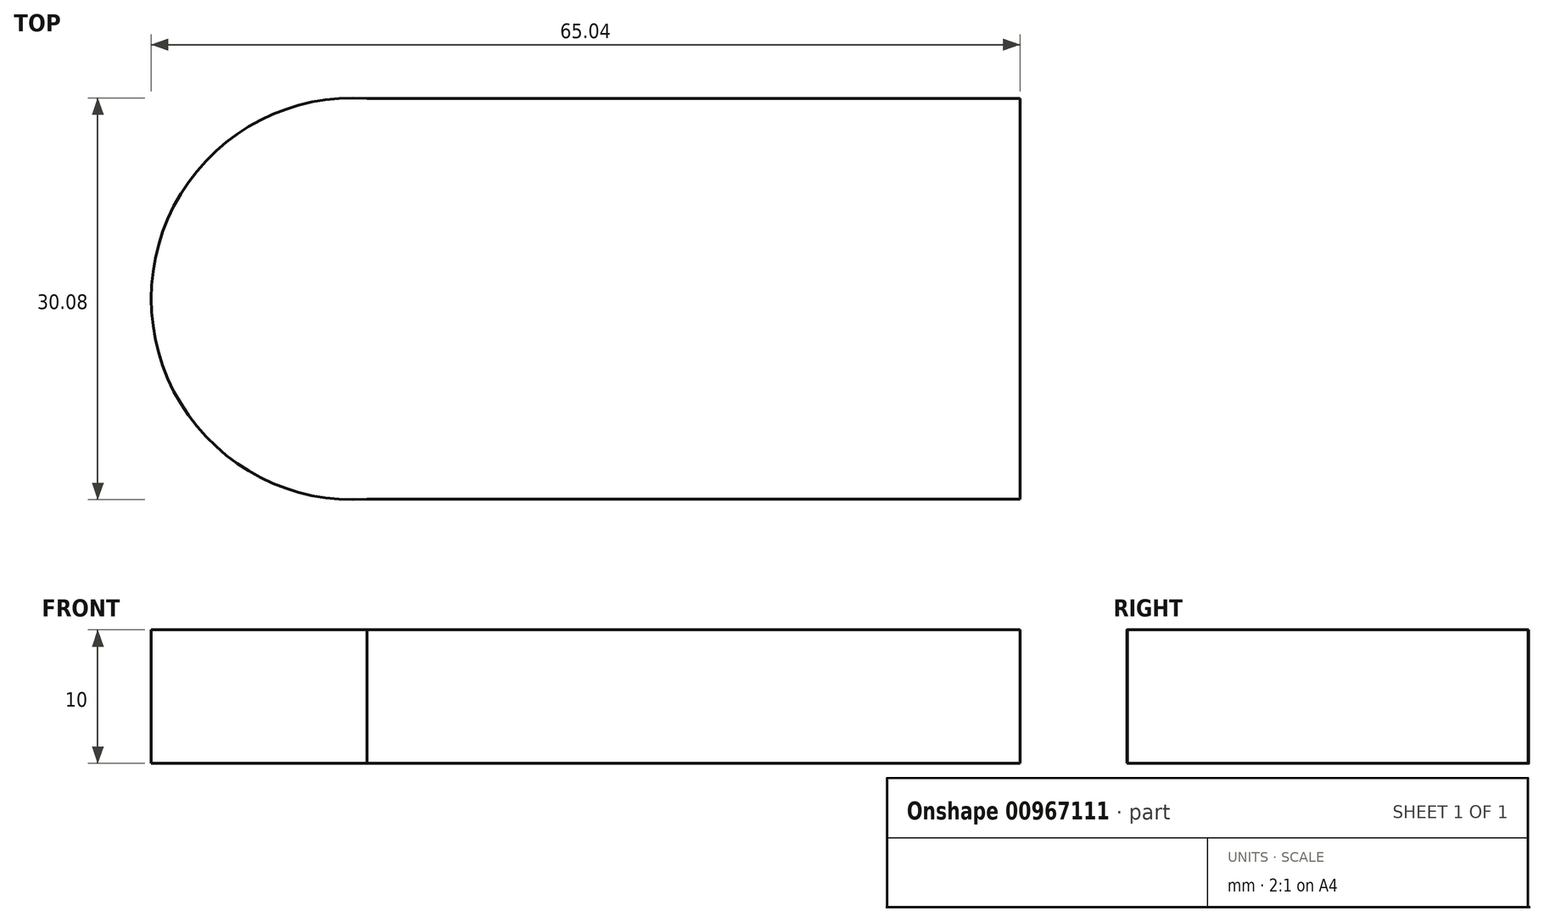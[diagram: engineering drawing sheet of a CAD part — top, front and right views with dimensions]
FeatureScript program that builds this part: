
annotation { "Feature Type Name" : "Feature", "Feature Type Description" : "" }
export const myFeature = defineFeature(function(context is Context, id is Id, definition is map)
    precondition{}
    {
        {
            var Q0;
            Q0=qCreatedBy(makeId("Top.planeOp"),FACE);
            var sketch = newSketch(context, id + "F0", { "sketchPlane" : qUnion([Q0])});
            skLineSegment(sketch, "E0.bottom", {"start": v(-27.78, 23.51) * mm, "end": v(22.22, 23.51) * mm});
            skLineSegment(sketch, "E0.top", {"start": v(-27.78, -6.49) * mm, "end": v(22.22, -6.49) * mm});
            skLineSegment(sketch, "E0.right", {"start": v(22.22, 23.51) * mm, "end": v(22.22, -6.49) * mm});
            skArc(sketch, "E1", {"start": v(-26.66, 23.51) * mm, "mid": v(-42.82, 8.51) * mm, "end": v(-26.66, -6.49) * mm});
            skSolve(sketch);
        }
        {
            var Q0;
            Q0 = qSketchRegion(id + "F0", true);
            extrude(context, id + "F1", {"entities" : qUnion([Q0]), "depth" : 10 * mm, "offsetDistance" : 25 * mm});
        }
    });
